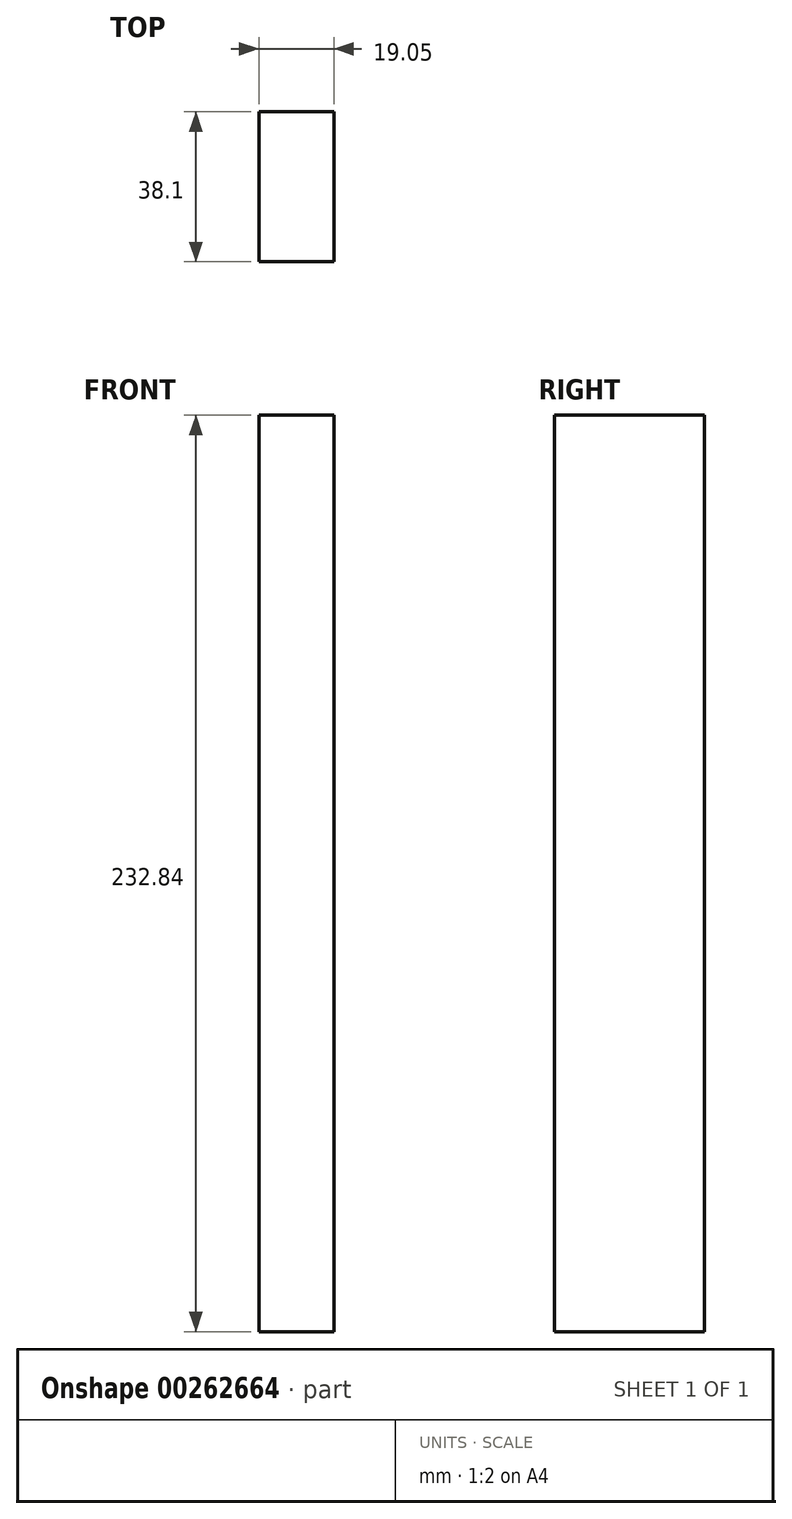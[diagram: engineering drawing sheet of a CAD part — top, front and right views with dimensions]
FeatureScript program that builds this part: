
annotation { "Feature Type Name" : "Feature", "Feature Type Description" : "" }
export const myFeature = defineFeature(function(context is Context, id is Id, definition is map)
    precondition{}
    {
        {
            var Q0;
            Q0=qCreatedBy(makeId("Front.planeOp"),FACE);
            var sketch = newSketch(context, id + "F0", { "sketchPlane" : qUnion([Q0])});
            skLineSegment(sketch, "E0", {"start": v(-19.05, -368.3) * mm, "end": v(0, -368.3) * mm});
            skLineSegment(sketch, "E1", {"start": v(0, -368.3) * mm, "end": v(0, -135.46) * mm});
            skLineSegment(sketch, "E2", {"start": v(-19.05, -135.46) * mm, "end": v(-19.05, -368.3) * mm});
            skLineSegment(sketch, "E3", {"start": v(-19.05, -135.46) * mm, "end": v(0, -135.46) * mm});
            skSolve(sketch);
        }
        {
            var Q0;
            Q0=makeQuery(id+"F0.imprint","IMPRINT",FACE,{"disambiguationData":[TD([[makeQuery(id+"F0.imprint","IMPRINT",EDGE,{"derivedFrom":sQuery(id+"F0.wireOp",EDGE,"E0")}),1.0]])]});
            extrude(context, id + "F1", {"entities" : qUnion([Q0]), "offsetDistance" : 25.4 * mm, "depth" : 38.1 * mm});
        }
    });
